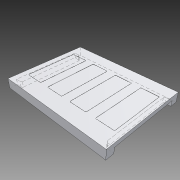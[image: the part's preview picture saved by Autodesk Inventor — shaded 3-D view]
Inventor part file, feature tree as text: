
AUTODESK INVENTOR PART (.ipt)
format: ipt  version: 2013 (Build 170138000, 138)  size: 163,328 bytes
history: native  units: mm
features: fillet x4, extrude x3, sketch x3
ambient origin geometry x8: Origin, YZ Plane, XZ Plane, XY Plane, X Axis, Y Axis, Z Axis, Center Point
bodies: Volumenkörper1 (feature_tree)
feature tree (10):
  extrude  "Extrusion1"  Depth=120.0mm
  extrude  "Extrusion2"  Depth=25.0mm
  extrude  "Extrusion3"  Depth=10.0mm
  fillet  "Rundung1"  Radius=60.0mm
  fillet  "Rundung2"  Radius=0.1mm
  fillet  "Rundung3"  Radius=40.0mm
  fillet  "Rundung4"  Radius=140.0mm
  sketch  "Skizze1"  dims[d0=160.0mm d1=120.0mm]
  sketch  "Skizze2"  dims[d2=14.0mm d3=0.0mm d4=25.0mm]
  sketch  "Skizze4"  dims[d5=75.0mm d6=10.0mm d7=60.0mm d15=0.1mm d16=0.0mm d45=40.0mm d47=38.333333mm d48=10.0mm d50=10.0mm d61=140.0mm d63=10.0mm d64=11.0mm d65=98.0mm d66=8.0mm d67=0.0mm d68=2.0mm d69=1.0mm d70=1.0mm d71=1.0mm]
